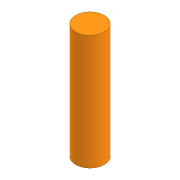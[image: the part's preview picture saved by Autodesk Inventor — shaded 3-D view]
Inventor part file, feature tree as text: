
AUTODESK INVENTOR PART (.ipt)
format: ipt  version: 2020.4 (Build 244396000, 396)  size: 74,240 bytes
history: native  units: in
note: dims shown in document units (in); Inventor stores cm internally (conversion verified against a paired STEP export)
features: extrude x1, sketch x1
ambient origin geometry x8: Origin, YZ Plane, XZ Plane, XY Plane, X Axis, Y Axis, Z Axis, Center Point
bodies: Solid1 (feature_tree)
feature tree (2):
  extrude  "Extrusion1"  Depth=4.0in TaperAngle=0.0deg
  sketch  "Sketch1"  dims[d0=1.0in d1=4.0in d2=0.0in]
